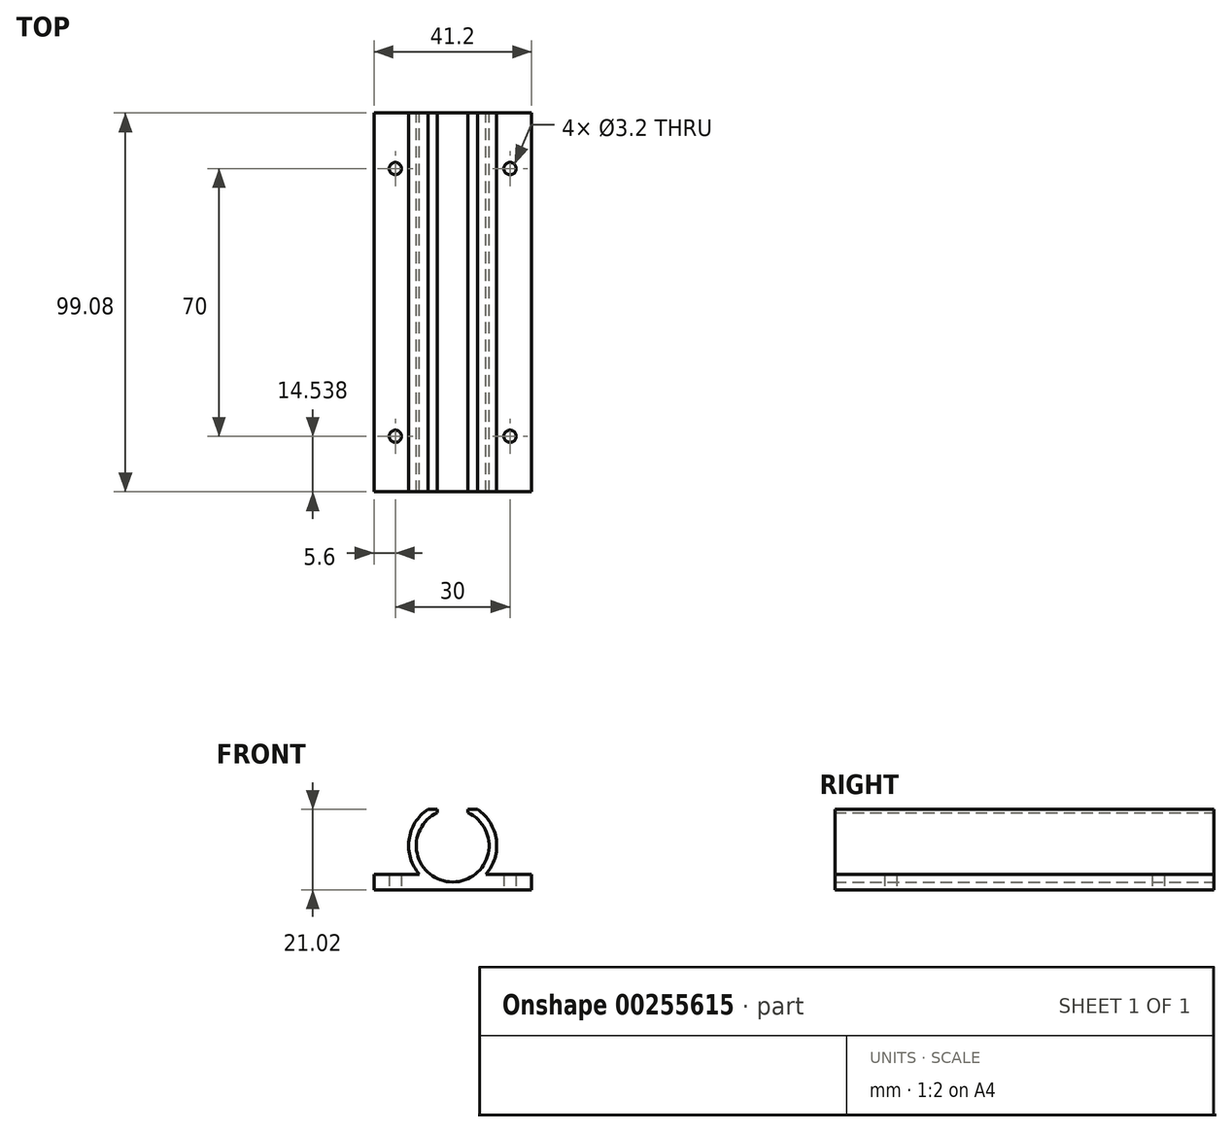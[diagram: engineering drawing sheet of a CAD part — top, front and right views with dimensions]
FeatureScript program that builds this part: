
annotation { "Feature Type Name" : "Feature", "Feature Type Description" : "" }
export const myFeature = defineFeature(function(context is Context, id is Id, definition is map)
    precondition{}
    {
        {
            var Q0;
            Q0=qCreatedBy(makeId("Front.planeOp"),FACE);
            var sketch = newSketch(context, id + "F0", { "sketchPlane" : qUnion([Q0])});
            skLineSegment(sketch, "E0.bottom", {"start": v(-20.6, 0) * mm, "end": v(20.6, 0) * mm});
            skLineSegment(sketch, "E0.top", {"start": v(-20.6, 4) * mm, "end": v(-8.72, 4) * mm});
            skLineSegment(sketch, "E0.left", {"start": v(-20.6, 0) * mm, "end": v(-20.6, 4) * mm});
            skLineSegment(sketch, "E0.right", {"start": v(20.6, 0) * mm, "end": v(20.6, 4) * mm});
            skArc(sketch, "E1", {"start": v(-4, 20.14) * mm, "mid": v(0, 2) * mm, "end": v(4, 20.14) * mm});
            skArc(sketch, "E2", {"start": v(-6.48, 21.02) * mm, "mid": v(-11.41, 13.01) * mm, "end": v(-8.72, 4) * mm});
            skLineSegment(sketch, "E3", {"start": v(-6.48, 21.02) * mm, "end": v(-4, 21.02) * mm});
            skLineSegment(sketch, "E4", {"start": v(-4, 21.02) * mm, "end": v(-4, 20.14) * mm});
            skLineSegment(sketch, "E5", {"start": v(4, 21.02) * mm, "end": v(4, 20.14) * mm});
            skLineSegment(sketch, "E6.trimOffspring", {"start": v(4, 21.02) * mm, "end": v(6.48, 21.02) * mm});
            skPoint(sketch, "E7.orphan", {"position": v(4, 17.43) * mm});
            skPoint(sketch, "E8.orphan", {"position": v(-4, 17.43) * mm});
            skLineSegment(sketch, "E9.trimOffspring", {"start": v(8.72, 4) * mm, "end": v(20.6, 4) * mm});
            skArc(sketch, "E10.trimOffspring", {"start": v(8.72, 4) * mm, "mid": v(11.41, 13.01) * mm, "end": v(6.48, 21.02) * mm});
            skLineSegment(sketch, "E11", {"start": v(-15, 7) * mm, "end": v(-15, -2.45) * mm, "construction": true});
            skLineSegment(sketch, "E12", {"start": v(15, 6.38) * mm, "end": v(15, -3.17) * mm, "construction": true});
            skLineSegment(sketch, "E13", {"start": v(-16.6, 7.05) * mm, "end": v(-16.6, -2.61) * mm, "construction": true});
            skLineSegment(sketch, "E14", {"start": v(-13.4, 7) * mm, "end": v(-13.4, -2.45) * mm, "construction": true});
            skSolve(sketch);
        }
        {
            var Q0;
            Q0=makeQuery(id+"F0.imprint","IMPRINT",FACE,{"disambiguationData":[TD([[makeQuery(id+"F0.imprint","IMPRINT",EDGE,{"derivedFrom":sQuery(id+"F0.wireOp",EDGE,"E0.bottom")}),1.0]])]});
            extrude(context, id + "F1", {"entities" : qUnion([Q0]), "depth" : 99.08 * mm});
        }
        {
            var Q0;
            Q0=makeQuery(id+"F1.opExtrude","SWEPT_FACE",FACE,{"disambiguationData":[OSD([sQuery(id+"F0.wireOp",EDGE,"E0.bottom")])]});
            var sketch = newSketch(context, id + "F2", { "sketchPlane" : qUnion([Q0])});
            skLineSegment(sketch, "E15.bottom", {"start": v(15, 84.54) * mm, "end": v(-15, 84.54) * mm, "construction": true});
            skLineSegment(sketch, "E15.top", {"start": v(15, 14.54) * mm, "end": v(-15, 14.54) * mm, "construction": true});
            skLineSegment(sketch, "E15.left", {"start": v(15, 84.54) * mm, "end": v(15, 14.54) * mm, "construction": true});
            skLineSegment(sketch, "E15.right", {"start": v(-15, 84.54) * mm, "end": v(-15, 14.54) * mm, "construction": true});
            skCircle(sketch, "E16", {"center": v(15, 84.54) * mm, "radius": 1.6 * mm});
            skCircle(sketch, "E17", {"center": v(-15, 84.54) * mm, "radius": 1.6 * mm});
            skCircle(sketch, "E18", {"center": v(15, 14.54) * mm, "radius": 1.6 * mm});
            skCircle(sketch, "E19", {"center": v(-15, 14.54) * mm, "radius": 1.6 * mm});
            skLineSegment(sketch, "E20", {"start": v(20.6, 49.54) * mm, "end": v(-20.6, 49.54) * mm, "construction": true});
            skSolve(sketch);
        }
        {
            var Q0;
            Q0 = qSketchRegion(id + "F2", true);
            extrude(context, id + "F3", {"entities" : qUnion([Q0]), "operationType" : NewBodyOperationType.REMOVE, "endBound" : BoundingType.THROUGH_ALL, "oppositeDirection" : true, "depth" : 25.4 * mm});
        }
    });
